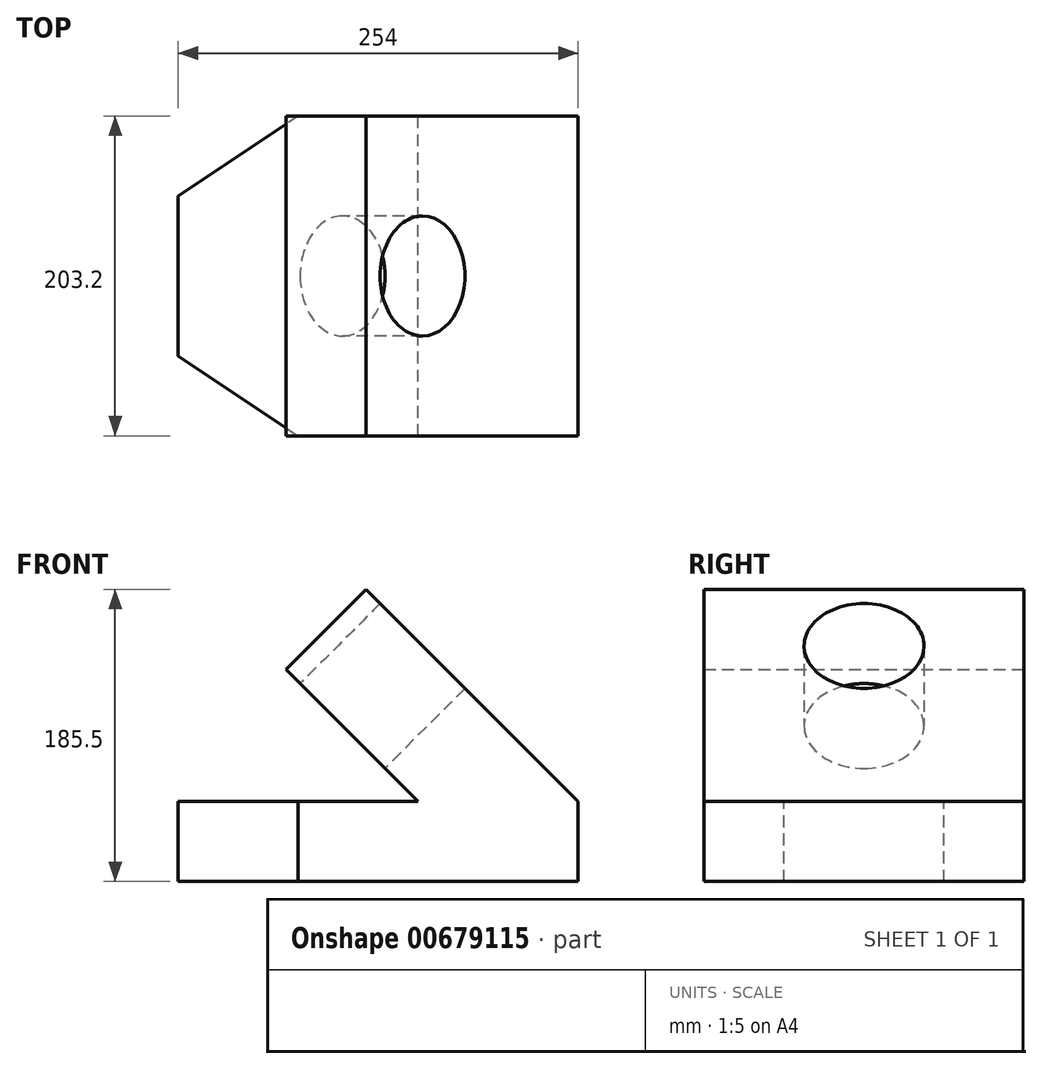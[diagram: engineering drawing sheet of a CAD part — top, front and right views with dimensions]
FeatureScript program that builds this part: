
annotation { "Feature Type Name" : "Feature", "Feature Type Description" : "" }
export const myFeature = defineFeature(function(context is Context, id is Id, definition is map)
    precondition{}
    {
        {
            var Q0;
            Q0=qCreatedBy(makeId("Front.planeOp"),FACE);
            var sketch = newSketch(context, id + "F0", { "sketchPlane" : qUnion([Q0])});
            skLineSegment(sketch, "E0", {"start": v(0, 0) * mm, "end": v(254, 0) * mm});
            skLineSegment(sketch, "E1", {"start": v(254, 0) * mm, "end": v(254, 50.8) * mm});
            skLineSegment(sketch, "E2", {"start": v(254, 50.8) * mm, "end": v(119.3, 185.5) * mm});
            skLineSegment(sketch, "E3", {"start": v(119.3, 185.5) * mm, "end": v(68.5, 134.7) * mm});
            skPoint(sketch, "E3.endSnap0", {"position": v(186.65, 118.15) * mm});
            skLineSegment(sketch, "E4", {"start": v(68.5, 134.7) * mm, "end": v(152.4, 50.8) * mm});
            skLineSegment(sketch, "E5", {"start": v(152.4, 50.8) * mm, "end": v(0, 50.8) * mm});
            skLineSegment(sketch, "E6", {"start": v(0, 50.8) * mm, "end": v(0, 0) * mm});
            skPoint(sketch, "E7.orphan", {"position": v(51.94, 118.15) * mm});
            skSolve(sketch);
        }
        {
            var Q0;
            Q0=makeQuery(id+"F0.imprint","IMPRINT",FACE,{"disambiguationData":[TD([[makeQuery(id+"F0.imprint","IMPRINT",EDGE,{"derivedFrom":sQuery(id+"F0.wireOp",EDGE,"E0")}),1.0]])]});
            extrude(context, id + "F1", {"entities" : qUnion([Q0]), "endBound" : BoundingType.SYMMETRIC, "depth" : 203.2 * mm, "offsetDistance" : 25.4 * mm});
        }
        {
            var Q0;
            Q0=makeQuery(id+"F1.opExtrude","SWEPT_FACE",FACE,{"disambiguationData":[OSD([sQuery(id+"F0.wireOp",EDGE,"E5")])]});
            var sketch = newSketch(context, id + "F2", { "sketchPlane" : qUnion([Q0])});
            skLineSegment(sketch, "E8", {"start": v(0, 101.6) * mm, "end": v(152.4, 101.6) * mm});
            skLineSegment(sketch, "E9", {"start": v(152.4, 101.6) * mm, "end": v(152.4, -101.6) * mm});
            skLineSegment(sketch, "E10", {"start": v(152.4, -101.6) * mm, "end": v(0, -101.6) * mm});
            skLineSegment(sketch, "E11", {"start": v(0, -101.6) * mm, "end": v(0, 101.6) * mm});
            skLineSegment(sketch, "E12", {"start": v(76.2, 101.6) * mm, "end": v(0, 50.8) * mm});
            skLineSegment(sketch, "E13", {"start": v(0, -50.8) * mm, "end": v(76.2, -101.6) * mm});
            skSolve(sketch);
        }
        {
            var Q0;
            {var subQ3=sQuery(id+"F2.wireOp",EDGE,"E12");Q0=makeQuery(id+"F2.imprint","IMPRINT",FACE,{"disambiguationData":[TD([[makeQuery(id+"F2.imprint","IMPRINT",EDGE,{"derivedFrom":subQ3}),-1.0]])]});}
            var Q1;
            {var subQ3=sQuery(id+"F2.wireOp",EDGE,"E13");Q1=makeQuery(id+"F2.imprint","IMPRINT",FACE,{"disambiguationData":[TD([[makeQuery(id+"F2.imprint","IMPRINT",EDGE,{"derivedFrom":subQ3}),-1.0]])]});}
            extrude(context, id + "F3", {"entities" : qUnion([Q0, Q1]), "operationType" : NewBodyOperationType.REMOVE, "endBound" : BoundingType.THROUGH_ALL, "oppositeDirection" : true, "depth" : 25.4 * mm, "offsetDistance" : 25.4 * mm});
        }
        {
            var Q0;
            Q0=makeQuery(id+"F1.opExtrude","SWEPT_FACE",FACE,{"disambiguationData":[OSD([sQuery(id+"F0.wireOp",EDGE,"E2")])]});
            cPlane(context, id + "F4", {"entities" : qUnion([Q0]), "cplaneType" : CPlaneType.OFFSET, "offset" : 25.4 * mm, "width" : 152.4 * mm, "height" : 152.4 * mm});
        }
        {
            var Q0;
            Q0=qCreatedBy(id+"F4.planeOp",FACE);
            var sketch = newSketch(context, id + "F5", { "sketchPlane" : qUnion([Q0])});
            skCircle(sketch, "E14", {"center": v(0, -3.98) * mm, "radius": 38.1 * mm});
            skSolve(sketch);
        }
        {
            var Q0;
            Q0=makeQuery(id+"F5.imprint","IMPRINT",FACE,{"disambiguationData":[TD([[makeQuery(id+"F5.imprint","IMPRINT",EDGE,{"derivedFrom":sQuery(id+"F5.wireOp",EDGE,"E14")}),1.0]])]});
            extrude(context, id + "F6", {"entities" : qUnion([Q0]), "operationType" : NewBodyOperationType.REMOVE, "depth" : 101.6 * mm, "offsetDistance" : 25.4 * mm, "hasSecondDirection" : true, "secondDirectionOppositeDirection" : true, "secondDirectionDepth" : 101.6 * mm});
        }
    });
